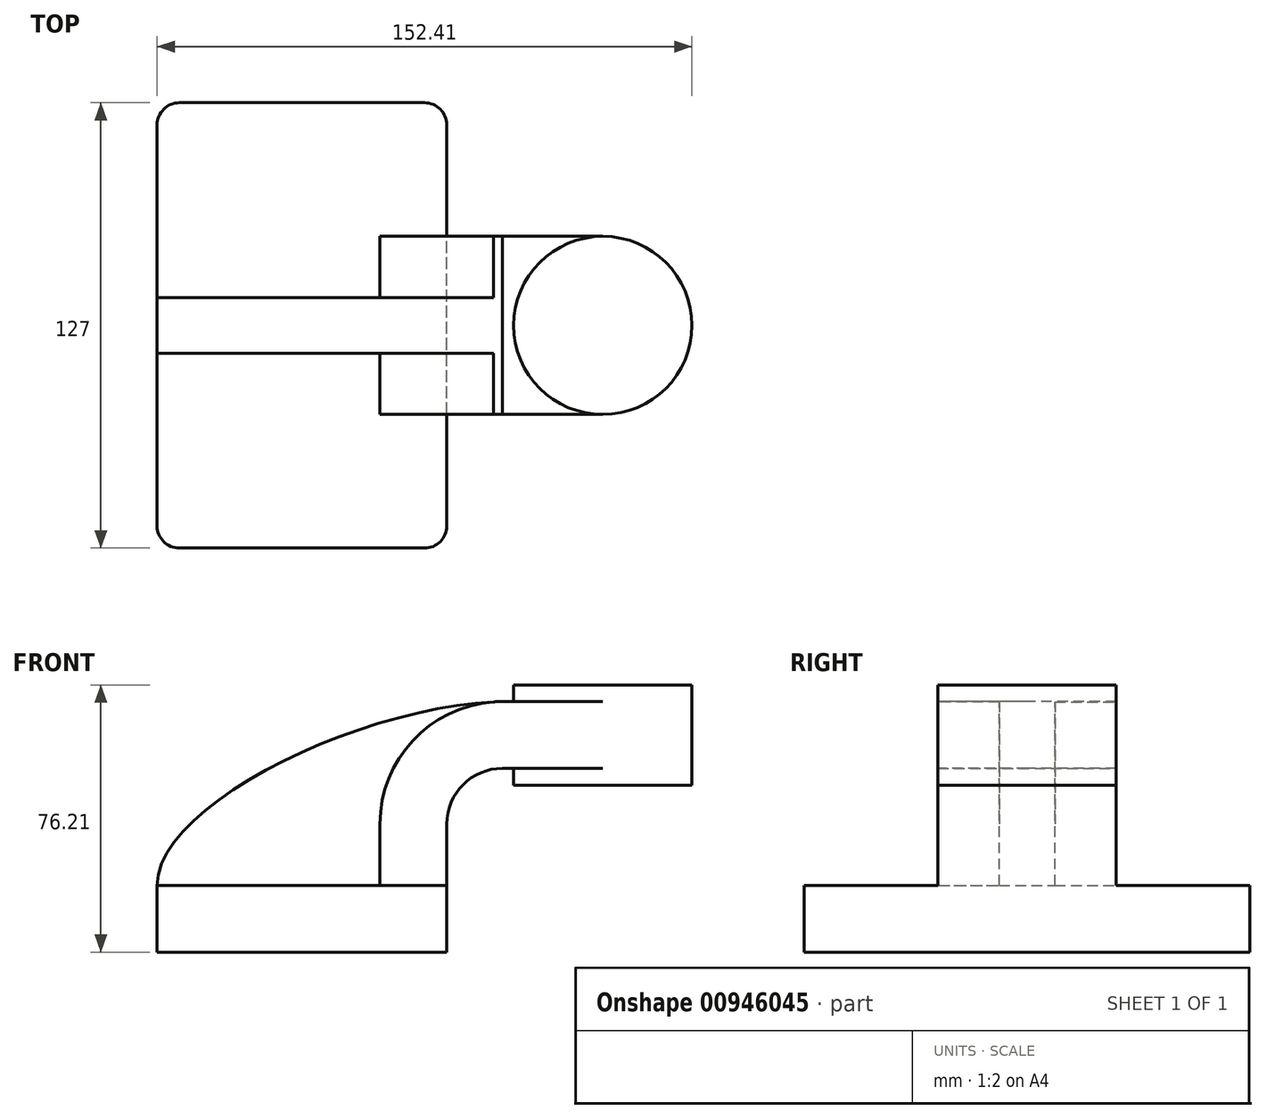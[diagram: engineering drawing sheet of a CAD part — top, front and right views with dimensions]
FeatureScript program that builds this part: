
annotation { "Feature Type Name" : "Feature", "Feature Type Description" : "" }
export const myFeature = defineFeature(function(context is Context, id is Id, definition is map)
    precondition{}
    {
        {
            var Q0;
            Q0=qCreatedBy(makeId("Front.planeOp"),FACE);
            var sketch = newSketch(context, id + "F0", { "sketchPlane" : qUnion([Q0])});
            skLineSegment(sketch, "E0.bottom", {"start": v(-41.28, 9.52) * mm, "end": v(41.27, 9.53) * mm});
            skLineSegment(sketch, "E0.top", {"start": v(-41.28, -9.53) * mm, "end": v(41.28, -9.53) * mm});
            skLineSegment(sketch, "E0.left", {"start": v(-41.28, 9.52) * mm, "end": v(-41.27, -9.53) * mm});
            skLineSegment(sketch, "E0.right", {"start": v(41.28, 9.53) * mm, "end": v(41.28, -9.52) * mm});
            skPoint(sketch, "E0.middle", {"position": v(0, 0) * mm});
            skLineSegment(sketch, "E1.bottom", {"start": v(60.32, 66.67) * mm, "end": v(111.12, 66.67) * mm});
            skLineSegment(sketch, "E1.top", {"start": v(60.33, 38.1) * mm, "end": v(111.12, 38.1) * mm});
            skLineSegment(sketch, "E1.left", {"start": v(60.32, 66.67) * mm, "end": v(60.33, 38.1) * mm});
            skLineSegment(sketch, "E1.right", {"start": v(111.12, 66.67) * mm, "end": v(111.12, 38.1) * mm});
            skPoint(sketch, "E1.middle", {"position": v(85.72, 52.39) * mm});
            skLineSegment(sketch, "E2", {"start": v(41.27, 9.53) * mm, "end": v(41.27, 27) * mm});
            skArc(sketch, "E3", {"start": v(41.27, 27) * mm, "mid": v(45.92, 38.23) * mm, "end": v(57.15, 42.88) * mm});
            skLineSegment(sketch, "E4", {"start": v(57.15, 42.88) * mm, "end": v(85.72, 42.88) * mm});
            skPoint(sketch, "E4.endSnap0", {"position": v(85.72, 38.1) * mm});
            skLineSegment(sketch, "E5.0", {"start": v(57.15, 61.93) * mm, "end": v(85.72, 61.93) * mm});
            skArc(sketch, "E5.1", {"start": v(22.22, 27) * mm, "mid": v(32.45, 51.7) * mm, "end": v(57.15, 61.93) * mm});
            skLineSegment(sketch, "E5.2", {"start": v(22.22, 9.53) * mm, "end": v(22.22, 27) * mm});
            skLineSegment(sketch, "E6", {"start": v(85.72, 38.1) * mm, "end": v(85.72, 66.67) * mm});
            skFitSpline(sketch, "E7", {"points": [v(-41.28, 9.53) * mm, v(57.15, 61.93) * mm], "startDerivative": vector(0.77, 70.97) * mm, "endDerivative": vector(117.51, 2.6) * mm});
            skSolve(sketch);
        }
        {
            var Q0;
            Q0=makeQuery(id+"F0.imprint","IMPRINT",FACE,{"disambiguationData":[TD([[makeQuery(id+"F0.imprint","IMPRINT",EDGE,{"derivedFrom":sQuery(id+"F0.wireOp",EDGE,"E0.top")}),1.0]])]});
            extrude(context, id + "F1", {"entities" : qUnion([Q0]), "endBound" : BoundingType.SYMMETRIC, "depth" : 127 * mm, "offsetDistance" : 25.4 * mm});
        }
        {
            var Q0;
            {var subQ1=sQuery(id+"F0.wireOp",EDGE,"E2");Q0=makeQuery(id+"F0.imprint","IMPRINT",FACE,{"disambiguationData":[TD([[makeQuery(id+"F0.imprint","IMPRINT",EDGE,{"derivedFrom":subQ1}),1.0]])]});}
            var Q1;
            {var subQ0=sQuery(id+"F0.wireOp",EDGE,"E5.0");var subQ1=sQuery(id+"F0.wireOp",EDGE,"E1.left");var subQ2=makeQuery(id+"F0.imprint","INTERSECT",VERTEX,{"derivedFrom":[subQ1,subQ0]});Q1=makeQuery(id+"F0.imprint","IMPRINT",FACE,{"disambiguationData":[TD([[makeQuery(id+"F0.imprint","IMPRINT",EDGE,{"disambiguationData":[TD([[subQ2,-1.0]])],"derivedFrom":subQ1}),1.0]])]});}
            extrude(context, id + "F2", {"entities" : qUnion([Q0, Q1]), "operationType" : NewBodyOperationType.ADD, "endBound" : BoundingType.SYMMETRIC, "depth" : 50.8 * mm, "offsetDistance" : 25.4 * mm});
        }
        {
            var Q0;
            {var subQ3=sQuery(id+"F0.wireOp",EDGE,"E5.2");Q0=makeQuery(id+"F0.imprint","IMPRINT",FACE,{"disambiguationData":[TD([[makeQuery(id+"F0.imprint","IMPRINT",EDGE,{"derivedFrom":subQ3}),1.0]])]});}
            extrude(context, id + "F3", {"entities" : qUnion([Q0]), "operationType" : NewBodyOperationType.ADD, "endBound" : BoundingType.SYMMETRIC, "depth" : 15.88 * mm, "offsetDistance" : 25.4 * mm});
        }
        {
            var Q0;
            {var subQ4=sQuery(id+"F0.wireOp",EDGE,"E1.right");Q0=makeQuery(id+"F0.imprint","IMPRINT",FACE,{"disambiguationData":[TD([[makeQuery(id+"F0.imprint","IMPRINT",EDGE,{"derivedFrom":subQ4}),-1.0]])]});}
            var Q1;
            Q1=sQuery(id+"F0.wireOp",EDGE,"E6");
            revolve(context, id + "F4", {"operationType" : NewBodyOperationType.ADD, "surfaceOperationType" : NewSurfaceOperationType.NEW, "entities" : qUnion([Q0]), "axis" : qUnion([Q1]), "revolveType" : RevolveType.FULL});
        }
        {
            var Q0;
            Q0=makeQuery(id+"F1.opExtrude","CAP_EDGE",EDGE,{"disambiguationData":[OSD([sQuery(id+"F0.wireOp",EDGE,"E0.right")])],"isStart":false});
            var Q1;
            Q1=makeQuery(id+"F1.opExtrude","CAP_EDGE",EDGE,{"disambiguationData":[OSD([sQuery(id+"F0.wireOp",EDGE,"E0.left")])],"isStart":false});
            var Q2;
            Q2=makeQuery(id+"F1.opExtrude","CAP_EDGE",EDGE,{"disambiguationData":[OSD([sQuery(id+"F0.wireOp",EDGE,"E0.left")])],"isStart":true});
            var Q3;
            Q3=makeQuery(id+"F1.opExtrude","CAP_EDGE",EDGE,{"disambiguationData":[OSD([sQuery(id+"F0.wireOp",EDGE,"E0.right")])],"isStart":true});
            fillet(context, id + "F5", {"entities" : qUnion([Q0, Q1, Q2, Q3]), "radius" : 6.35 * mm, "tangentPropagation" : true, "allowEdgeOverflow" : false});
        }
    });
